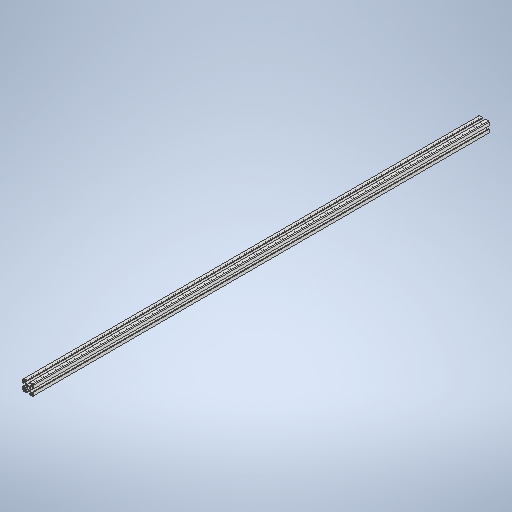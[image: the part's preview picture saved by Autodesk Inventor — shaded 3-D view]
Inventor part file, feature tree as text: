
AUTODESK INVENTOR PART (.ipt)
format: ipt  version: 2025 (Build 290162000, 162)  size: 315,904 bytes
history: native  units: in
note: dims shown in document units (in); Inventor stores cm internally (conversion verified against a paired STEP export)
features: extrude x1, sketch x1
ambient origin geometry x8: Origin, YZ Plane, XZ Plane, XY Plane, X Axis, Y Axis, Z Axis, Center Point
bodies: Solid1 (feature_tree)
feature tree (2):
  extrude  "Extrusion1"  Depth=50.7874in
  sketch  "Sketch1"  dims[d6=50.7874in d7=0.0in d8=0.1969in d9=0.0344in]
